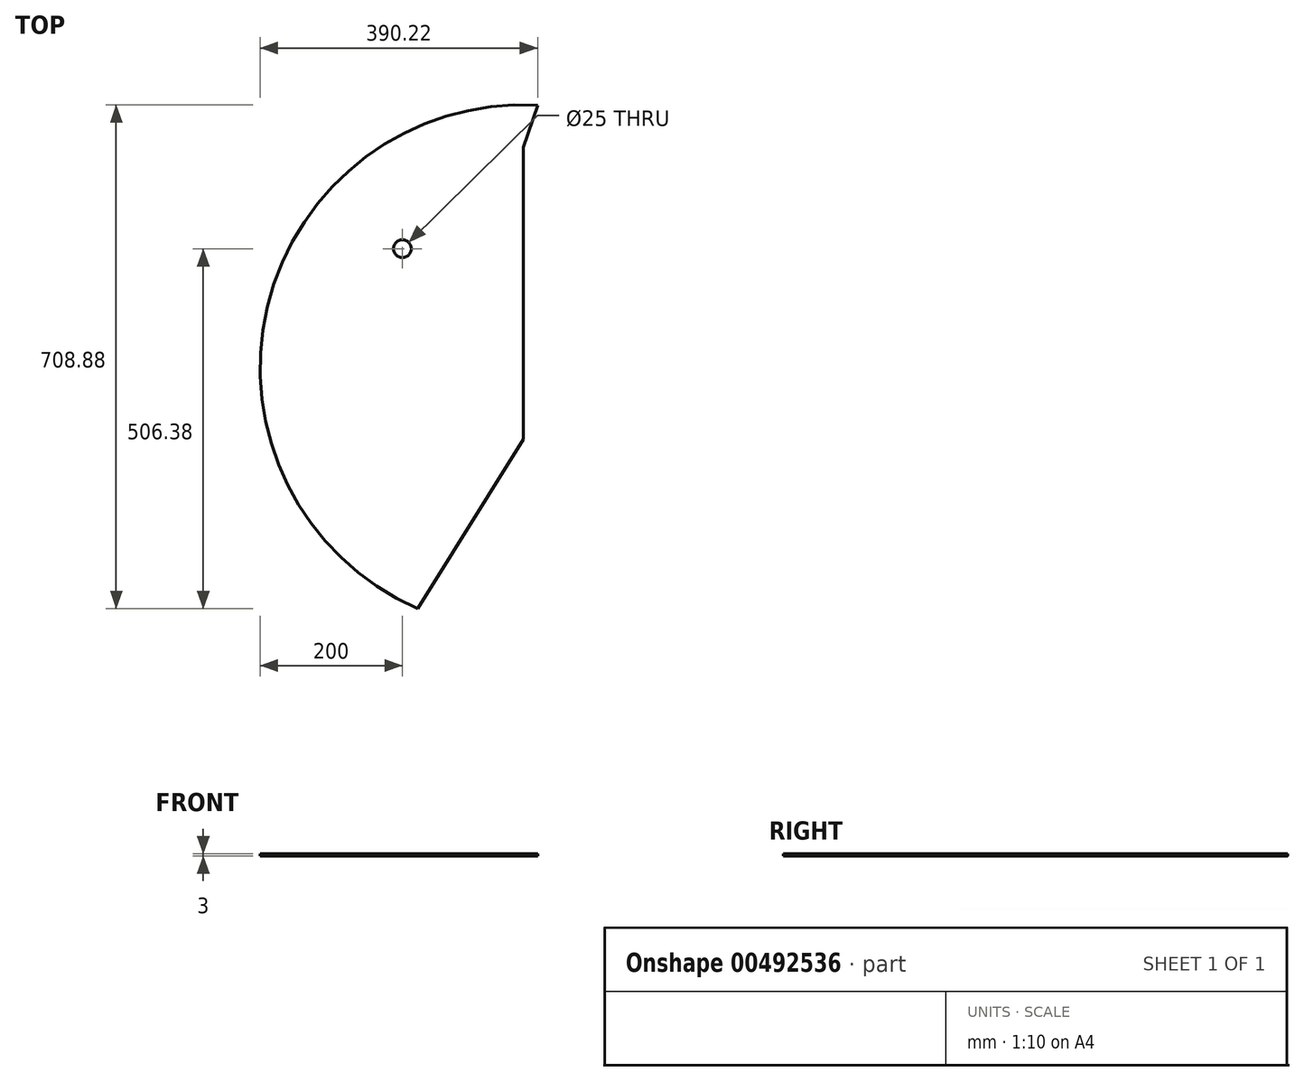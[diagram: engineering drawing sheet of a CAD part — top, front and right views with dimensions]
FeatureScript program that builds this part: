
annotation { "Feature Type Name" : "Feature", "Feature Type Description" : "" }
export const myFeature = defineFeature(function(context is Context, id is Id, definition is map)
    precondition{}
    {
        {
            var Q0;
            Q0=qCreatedBy(makeId("Top.planeOp"),FACE);
            var sketch = newSketch(context, id + "F0", { "sketchPlane" : qUnion([Q0])});
            skArc(sketch, "E0", {"start": v(2.35, 474.07) * mm, "mid": v(-377.8, 190.37) * mm, "end": v(-166.4, -234.26) * mm});
            skLineSegment(sketch, "E1", {"start": v(-17.87, 104.62) * mm, "end": v(-17.87, 414.62) * mm});
            skLineSegment(sketch, "E2", {"start": v(-17.87, 104.62) * mm, "end": v(-17.87, 3.66) * mm});
            skLineSegment(sketch, "E3", {"start": v(-17.87, 3.66) * mm, "end": v(-166.4, -234.26) * mm});
            skLineSegment(sketch, "E4", {"start": v(2.35, 474.07) * mm, "end": v(-17.87, 414.62) * mm});
            skCircle(sketch, "E5", {"center": v(-187.87, 272.12) * mm, "radius": 12.5 * mm});
            skSolve(sketch);
        }
        {
            var Q0;
            Q0=qSketchRegion(id+"F0",true);
            extrude(context, id + "F1", {"entities" : qUnion([Q0]), "depth" : 3 * mm});
        }
    });
